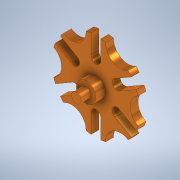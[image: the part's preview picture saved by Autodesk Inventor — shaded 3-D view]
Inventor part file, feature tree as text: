
AUTODESK INVENTOR PART (.ipt)
format: ipt  version: 2022 (Build 260153000, 153)  size: 201,216 bytes
history: native  units: in
note: dims shown in document units (in); Inventor stores cm internally (conversion verified against a paired STEP export)
features: sketch x4, extrude x3, mirror x1, pattern_circular x1
ambient origin geometry x8: Origin, YZ Plane, XZ Plane, XY Plane, X Axis, Y Axis, Z Axis, Center Point
bodies: Solid1 (feature_tree)
feature tree (9):
  sketch  "Sketch1"  dims[d0=1.7717in d1=0.5906in d3=30.0deg]
  extrude  "Extrusion1"  Depth=0.5906in TaperAngle=30.0deg
  mirror  "Mirror1"
  pattern_circular  "Circular Pattern1"  Count=5  [1 undecoded]
  extrude  "Extrusion2"  Depth=1.7717in
  extrude  "Extrusion3"  Depth=0.5906in
  sketch  "Sketch2"  dims[d4=0.1969in]
  sketch  "Sketch3"  dims[d5=0.9843in]
  sketch  "Sketch4"  dims[d6=30.0deg d7=1.9685in d8=1.7717in d9=0.5906in d10=0.315in d11=0.0in d12=2.3622in d13=360.0deg d15=0.3937in d16=0.3937in d17=0.0in d18=0.1969in d19=0.3937in d20=0.0in]
note: 1 required parameter value undecoded (feature->parameter linkage not recoverable at this tier; creation-order binding heuristic only, values carry confidence <= 0.55)
